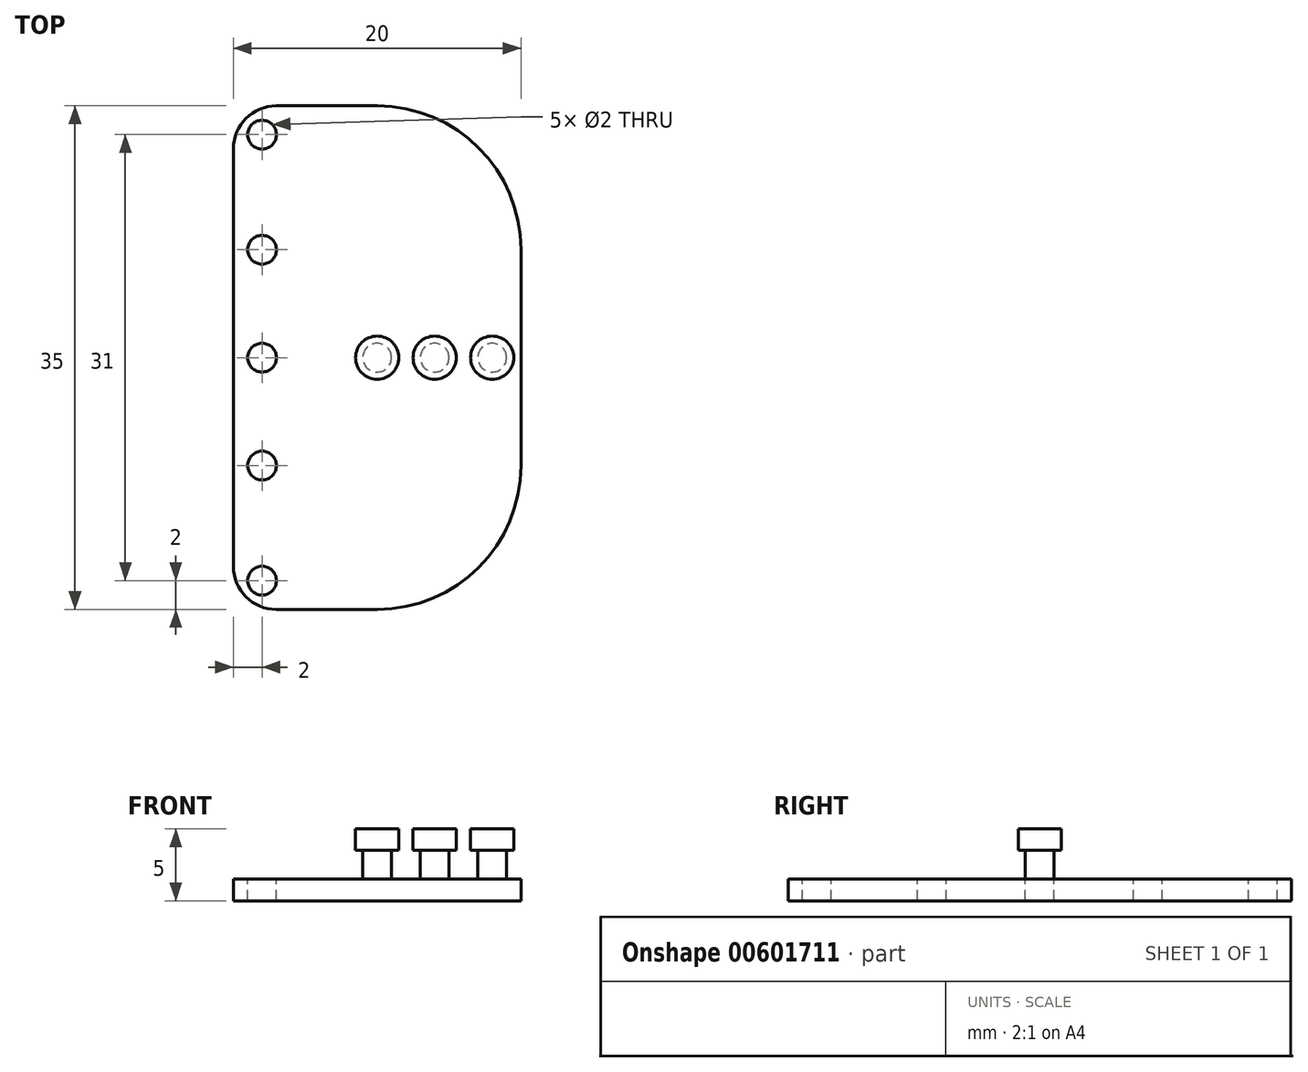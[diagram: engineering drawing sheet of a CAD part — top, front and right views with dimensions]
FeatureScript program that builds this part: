
annotation { "Feature Type Name" : "Feature", "Feature Type Description" : "" }
export const myFeature = defineFeature(function(context is Context, id is Id, definition is map)
    precondition{}
    {
        {
            var Q0;
            Q0=qCreatedBy(makeId("Top.planeOp"),FACE);
            var sketch = newSketch(context, id + "F0", { "sketchPlane" : qUnion([Q0])});
            skLineSegment(sketch, "E0.bottom", {"start": v(-10, 17.5) * mm, "end": v(10, 17.5) * mm});
            skLineSegment(sketch, "E0.top", {"start": v(-10, -17.5) * mm, "end": v(10, -17.5) * mm});
            skLineSegment(sketch, "E0.left", {"start": v(-10, 17.5) * mm, "end": v(-10, -17.5) * mm});
            skLineSegment(sketch, "E0.right", {"start": v(10, 17.5) * mm, "end": v(10, -17.5) * mm});
            skSolve(sketch);
        }
        {
            var Q0;
            Q0=makeQuery(id+"F0.imprint","IMPRINT",FACE,{"disambiguationData":[TD([[makeQuery(id+"F0.imprint","IMPRINT",EDGE,{"derivedFrom":sQuery(id+"F0.wireOp",EDGE,"E0.bottom")}),-1.0]])]});
            extrude(context, id + "F1", {"entities" : qUnion([Q0]), "oppositeDirection" : true, "depth" : 1.5 * mm, "offsetDistance" : 25 * mm});
        }
        {
            var Q0;
            Q0=makeQuery(id+"F1.opExtrude","CAP_FACE",FACE,{"disambiguationData":[OSD([sQuery(id+"F0.wireOp",EDGE,"E0.bottom"),sQuery(id+"F0.wireOp",EDGE,"E0.top"),sQuery(id+"F0.wireOp",EDGE,"E0.left"),sQuery(id+"F0.wireOp",EDGE,"E0.right"),sQuery(id+"F0.wireOp",EDGE,"KmeBwiC0-vNsX-GSjz-3H2x-m4VyhV1g3tne.bottom"),sQuery(id+"F0.wireOp",EDGE,"KmeBwiC0-vNsX-GSjz-3H2x-m4VyhV1g3tne.top"),sQuery(id+"F0.wireOp",EDGE,"KmeBwiC0-vNsX-GSjz-3H2x-m4VyhV1g3tne.left"),sQuery(id+"F0.wireOp",EDGE,"KmeBwiC0-vNsX-GSjz-3H2x-m4VyhV1g3tne.right")])],"isStart":true});
            var sketch = newSketch(context, id + "F2", { "sketchPlane" : qUnion([Q0])});
            skLineSegment(sketch, "E1", {"start": v(-8, 22.16) * mm, "end": v(-8, -20.94) * mm, "construction": true});
            skCircle(sketch, "E2", {"center": v(-8, 0) * mm, "radius": 1 * mm});
            skCircle(sketch, "E3", {"center": v(-8, 15.5) * mm, "radius": 1 * mm});
            skCircle(sketch, "E4", {"center": v(-8, 7.5) * mm, "radius": 1 * mm});
            skCircle(sketch, "E5", {"center": v(-8, -15.5) * mm, "radius": 1 * mm});
            skCircle(sketch, "E6", {"center": v(-8, -7.5) * mm, "radius": 1 * mm});
            skSolve(sketch);
        }
        {
            var Q0;
            Q0=makeQuery(id+"F2.imprint","IMPRINT",FACE,{"disambiguationData":[TD([[makeQuery(id+"F2.imprint","IMPRINT",EDGE,{"derivedFrom":sQuery(id+"F2.wireOp",EDGE,"E3")}),1.0]])]});
            var Q1;
            Q1=makeQuery(id+"F2.imprint","IMPRINT",FACE,{"disambiguationData":[TD([[makeQuery(id+"F2.imprint","IMPRINT",EDGE,{"derivedFrom":sQuery(id+"F2.wireOp",EDGE,"E4")}),1.0]])]});
            var Q2;
            Q2=makeQuery(id+"F2.imprint","IMPRINT",FACE,{"disambiguationData":[TD([[makeQuery(id+"F2.imprint","IMPRINT",EDGE,{"derivedFrom":sQuery(id+"F2.wireOp",EDGE,"E2")}),1.0]])]});
            var Q3;
            Q3=makeQuery(id+"F2.imprint","IMPRINT",FACE,{"disambiguationData":[TD([[makeQuery(id+"F2.imprint","IMPRINT",EDGE,{"derivedFrom":sQuery(id+"F2.wireOp",EDGE,"E6")}),1.0]])]});
            var Q4;
            Q4=makeQuery(id+"F2.imprint","IMPRINT",FACE,{"disambiguationData":[TD([[makeQuery(id+"F2.imprint","IMPRINT",EDGE,{"derivedFrom":sQuery(id+"F2.wireOp",EDGE,"E5")}),1.0]])]});
            extrude(context, id + "F3", {"entities" : qUnion([Q0, Q1, Q2, Q3, Q4]), "operationType" : NewBodyOperationType.REMOVE, "oppositeDirection" : true, "depth" : 1.5 * mm, "offsetDistance" : 25 * mm});
        }
        {
            var Q0;
            Q0=makeQuery(id+"F1.opExtrude","SWEPT_EDGE",EDGE,{"disambiguationData":[OSD([sQuery(id+"F0.wireOp",EDGE,"E0.top"),sQuery(id+"F0.wireOp",EDGE,"E0.left")])]});
            var Q1;
            Q1=makeQuery(id+"F1.opExtrude","SWEPT_EDGE",EDGE,{"disambiguationData":[OSD([sQuery(id+"F0.wireOp",EDGE,"E0.bottom"),sQuery(id+"F0.wireOp",EDGE,"E0.left")])]});
            fillet(context, id + "F4", {"entities" : qUnion([Q0, Q1]), "radius" : 3 * mm, "tangentPropagation" : true, "allowEdgeOverflow" : false});
        }
        {
            var Q0;
            Q0=makeQuery(id+"F1.opExtrude","SWEPT_EDGE",EDGE,{"disambiguationData":[OSD([sQuery(id+"F0.wireOp",EDGE,"E0.bottom"),sQuery(id+"F0.wireOp",EDGE,"E0.right")])]});
            var Q1;
            Q1=makeQuery(id+"F1.opExtrude","SWEPT_EDGE",EDGE,{"disambiguationData":[OSD([sQuery(id+"F0.wireOp",EDGE,"E0.top"),sQuery(id+"F0.wireOp",EDGE,"E0.right")])]});
            fillet(context, id + "F5", {"entities" : qUnion([Q0, Q1]), "radius" : 10 * mm, "tangentPropagation" : true, "allowEdgeOverflow" : false});
        }
        {
            var Q0;
            Q0=makeQuery(id+"F1.opExtrude","CAP_FACE",FACE,{"disambiguationData":[OSD([sQuery(id+"F0.wireOp",EDGE,"E0.bottom"),sQuery(id+"F0.wireOp",EDGE,"E0.top"),sQuery(id+"F0.wireOp",EDGE,"E0.left"),sQuery(id+"F0.wireOp",EDGE,"E0.right")])],"isStart":true});
            var sketch = newSketch(context, id + "F6", { "sketchPlane" : qUnion([Q0])});
            skCircle(sketch, "E7", {"center": v(8, 0) * mm, "radius": 1 * mm});
            skCircle(sketch, "E8", {"center": v(4, 0) * mm, "radius": 1 * mm});
            skCircle(sketch, "E9", {"center": v(0, 0) * mm, "radius": 1 * mm});
            skSolve(sketch);
        }
        {
            var Q0;
            Q0=makeQuery(id+"F6.imprint","IMPRINT",FACE,{"disambiguationData":[TD([[makeQuery(id+"F6.imprint","IMPRINT",EDGE,{"derivedFrom":sQuery(id+"F6.wireOp",EDGE,"E9")}),1.0]])]});
            var Q1;
            Q1=makeQuery(id+"F6.imprint","IMPRINT",FACE,{"disambiguationData":[TD([[makeQuery(id+"F6.imprint","IMPRINT",EDGE,{"derivedFrom":sQuery(id+"F6.wireOp",EDGE,"E8")}),1.0]])]});
            var Q2;
            Q2=makeQuery(id+"F6.imprint","IMPRINT",FACE,{"disambiguationData":[TD([[makeQuery(id+"F6.imprint","IMPRINT",EDGE,{"derivedFrom":sQuery(id+"F6.wireOp",EDGE,"E7")}),1.0]])]});
            extrude(context, id + "F7", {"entities" : qUnion([Q0, Q1, Q2]), "operationType" : NewBodyOperationType.ADD, "depth" : 2 * mm, "offsetDistance" : 25 * mm});
        }
        {
            var Q0;
            Q0=makeQuery(id+"F7.opExtrude","CAP_FACE",FACE,{"disambiguationData":[OSD([sQuery(id+"F6.wireOp",EDGE,"E9")])],"isStart":false});
            var sketch = newSketch(context, id + "F8", { "sketchPlane" : qUnion([Q0])});
            skCircle(sketch, "E10", {"center": v(0, 0) * mm, "radius": 1.5 * mm});
            skCircle(sketch, "E11", {"center": v(4, 0) * mm, "radius": 1.5 * mm});
            skCircle(sketch, "E12", {"center": v(8, 0) * mm, "radius": 1.5 * mm});
            skSolve(sketch);
        }
        {
            var Q0;
            Q0=makeQuery(id+"F8.imprint","IMPRINT",FACE,{"disambiguationData":[TD([[makeQuery(id+"F8.imprint","IMPRINT",EDGE,{"derivedFrom":makeQuery(id+"F7.opExtrude","CAP_EDGE",EDGE,{"disambiguationData":[OSD([sQuery(id+"F6.wireOp",EDGE,"E9")])],"isStart":false})}),1.0]])]});
            var Q1;
            Q1=makeQuery(id+"F8.imprint","IMPRINT",FACE,{"disambiguationData":[TD([[makeQuery(id+"F8.imprint","IMPRINT",EDGE,{"derivedFrom":sQuery(id+"F8.wireOp",EDGE,"E10")}),1.0]])]});
            var Q2;
            Q2=makeQuery(id+"F8.imprint","IMPRINT",FACE,{"disambiguationData":[TD([[makeQuery(id+"F8.imprint","IMPRINT",EDGE,{"derivedFrom":sQuery(id+"F8.wireOp",EDGE,"E11")}),1.0]])]});
            var Q3;
            Q3=makeQuery(id+"F8.imprint","IMPRINT",FACE,{"disambiguationData":[TD([[makeQuery(id+"F8.imprint","IMPRINT",EDGE,{"derivedFrom":sQuery(id+"F8.wireOp",EDGE,"E12")}),1.0]])]});
            extrude(context, id + "F9", {"entities" : qUnion([Q0, Q1, Q2, Q3]), "operationType" : NewBodyOperationType.ADD, "depth" : 1.5 * mm, "offsetDistance" : 25 * mm});
        }
    });
